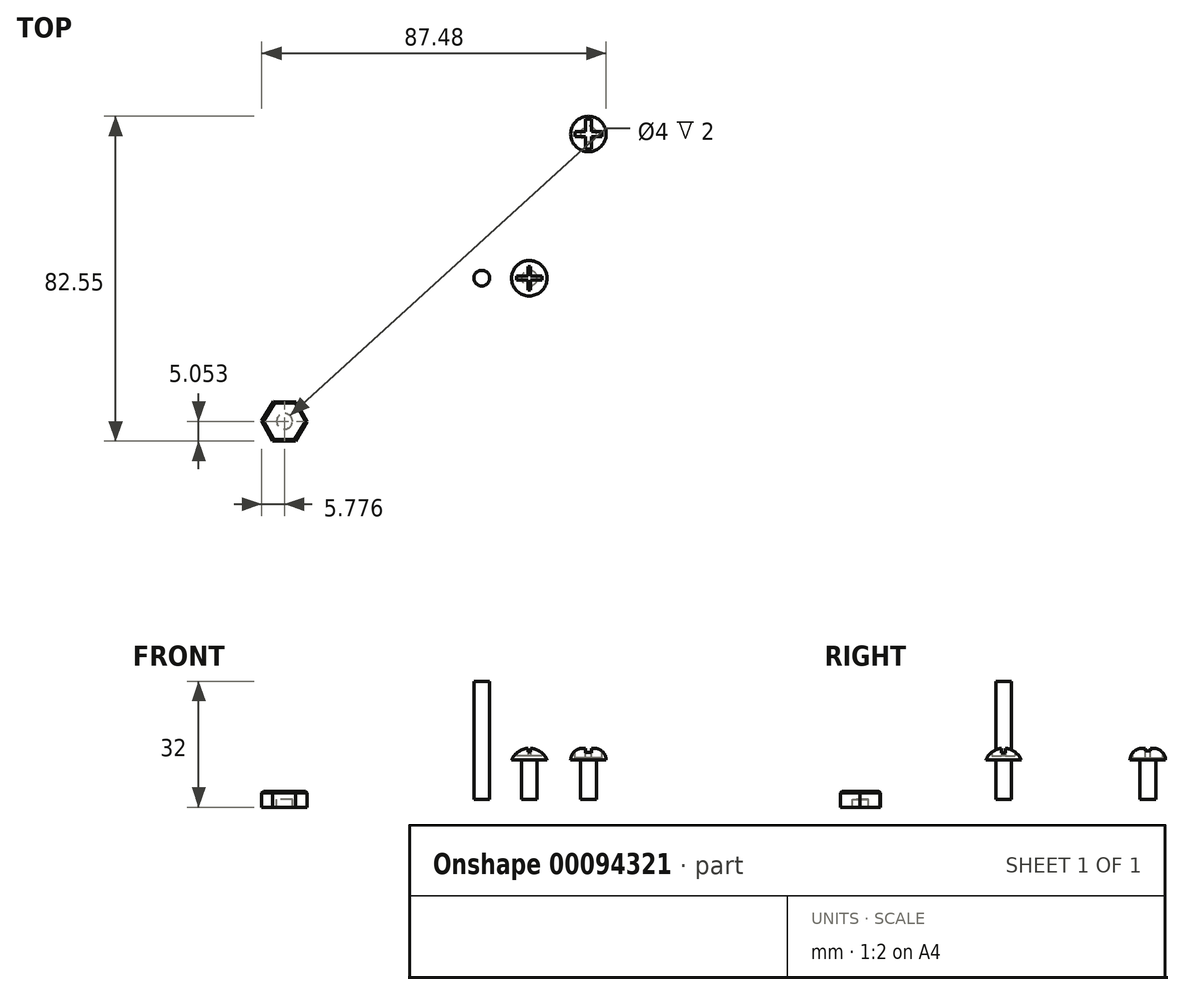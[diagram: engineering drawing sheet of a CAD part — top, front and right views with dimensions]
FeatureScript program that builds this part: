
annotation { "Feature Type Name" : "Feature", "Feature Type Description" : "" }
export const myFeature = defineFeature(function(context is Context, id is Id, definition is map)
    precondition{}
    {
        {
            var Q0;
            Q0=qCreatedBy(makeId("Top.planeOp"),FACE);
            var sketch = newSketch(context, id + "F0", { "sketchPlane" : qUnion([Q0])});
            skCircle(sketch, "E0", {"center": v(0, 0) * mm, "radius": 2 * mm});
            skSolve(sketch);
        }
        {
            var Q0;
            Q0 = qSketchRegion(id + "F0", true);
            extrude(context, id + "F1", {"entities" : qUnion([Q0]), "depth" : 30 * mm});
        }
        {
            var Q0;
            Q0=qCreatedBy(makeId("Top.planeOp"),FACE);
            var sketch = newSketch(context, id + "F2", { "sketchPlane" : qUnion([Q0])});
            skCircle(sketch, "E1.cCircle", {"center": v(-50.11, -36.36) * mm, "radius": 5 * mm, "construction": true});
            skLineSegment(sketch, "E1.0", {"start": v(-47.13, -31.41) * mm, "end": v(-44.34, -36.47) * mm});
            skLineSegment(sketch, "E1.1", {"start": v(-44.34, -36.47) * mm, "end": v(-47.32, -41.41) * mm});
            skLineSegment(sketch, "E1.2", {"start": v(-47.32, -41.41) * mm, "end": v(-53.1, -41.3) * mm});
            skLineSegment(sketch, "E1.3", {"start": v(-53.1, -41.3) * mm, "end": v(-55.89, -36.24) * mm});
            skLineSegment(sketch, "E1.4", {"start": v(-55.89, -36.24) * mm, "end": v(-52.9, -31.3) * mm});
            skLineSegment(sketch, "E1.5", {"start": v(-52.9, -31.3) * mm, "end": v(-47.13, -31.41) * mm});
            skPoint(sketch, "E1.0.midPoint", {"position": v(-45.74, -33.94) * mm});
            skSolve(sketch);
        }
        {
            var Q0;
            Q0 = qSketchRegion(id + "F2", true);
            extrude(context, id + "F3", {"entities" : qUnion([Q0]), "endBound" : BoundingType.SYMMETRIC, "oppositeDirection" : true, "depth" : 4 * mm});
        }
        {
            var Q0;
            Q0=makeQuery(id+"F3.opExtrude","CAP_FACE",FACE,{"disambiguationData":[OSD([sQuery(id+"F2.wireOp",EDGE,"E1.0"),sQuery(id+"F2.wireOp",EDGE,"E1.1"),sQuery(id+"F2.wireOp",EDGE,"E1.2"),sQuery(id+"F2.wireOp",EDGE,"E1.3"),sQuery(id+"F2.wireOp",EDGE,"E1.4"),sQuery(id+"F2.wireOp",EDGE,"E1.5")])],"isStart":true});
            var sketch = newSketch(context, id + "F4", { "sketchPlane" : qUnion([Q0])});
            skArc(sketch, "E2", {"start": v(-50.11, -40.36) * mm, "mid": v(-46.11, -36.36) * mm, "end": v(-50.11, -32.36) * mm});
            skLineSegment(sketch, "E3", {"start": v(-50.11, -32.36) * mm, "end": v(-50.11, -40.36) * mm, "construction": true});
            skSolve(sketch);
        }
        {
            var Q0;
            Q0=sQuery(id+"F4.wireOp",EDGE,"E2");
            var Q1;
            Q1=sQuery(id+"F4.wireOp",EDGE,"E3");
            revolve(context, id + "F5", {"bodyType" : ToolBodyType.SURFACE, "surfaceEntities" : qUnion([Q0]), "axis" : qUnion([Q1]), "revolveType" : RevolveType.ONE_DIRECTION, "angle" : 180 * degree});
        }
        {
            var Q0;
            Q0=makeQuery(id+"F2.imprint","IMPRINT",FACE,{"disambiguationData":[TD([[makeQuery(id+"F2.imprint","IMPRINT",EDGE,{"derivedFrom":sQuery(id+"F2.wireOp",EDGE,"E1.0")}),-1.0]])]});
            var sketch = newSketch(context, id + "F6", { "sketchPlane" : qUnion([Q0])});
            skCircle(sketch, "E4", {"center": v(-50.11, -36.36) * mm, "radius": 2 * mm});
            skSolve(sketch);
        }
        {
            var Q0;
            Q0 = qSketchRegion(id + "F6", true);
            extrude(context, id + "F7", {"entities" : qUnion([Q0]), "operationType" : NewBodyOperationType.REMOVE, "oppositeDirection" : true, "depth" : 25 * mm});
        }
        {
            var Q0;
            Q0=qCreatedBy(makeId("Top.planeOp"),FACE);
            var sketch = newSketch(context, id + "F8", { "sketchPlane" : qUnion([Q0])});
            skCircle(sketch, "E5", {"center": v(27.1, 36.64) * mm, "radius": 2 * mm});
            skSolve(sketch);
        }
        {
            var Q0;
            Q0 = qSketchRegion(id + "F8", true);
            extrude(context, id + "F9", {"entities" : qUnion([Q0]), "depth" : 10 * mm});
        }
        {
            var Q0;
            Q0=makeQuery(id+"F9.opExtrude","CAP_FACE",FACE,{"disambiguationData":[OSD([sQuery(id+"F8.wireOp",EDGE,"E5")])],"isStart":false});
            var sketch = newSketch(context, id + "F10", { "sketchPlane" : qUnion([Q0])});
            skCircle(sketch, "E6", {"center": v(27.1, 36.64) * mm, "radius": 4.5 * mm});
            skSolve(sketch);
        }
        {
            var Q0;
            Q0 = qSketchRegion(id + "F10", true);
            extrude(context, id + "F11", {"entities" : qUnion([Q0]), "operationType" : NewBodyOperationType.ADD, "depth" : 3 * mm});
        }
        {
            var Q0;
            Q0=makeQuery(id+"F11.opExtrude","CAP_EDGE",EDGE,{"disambiguationData":[OSD([sQuery(id+"F10.wireOp",EDGE,"E6")])],"isStart":false});
            fillet(context, id + "F12", {"entities" : qUnion([Q0]), "radius" : 3 * mm, "tangentPropagation" : true, "allowEdgeOverflow" : false});
        }
        {
            var Q0;
            Q0=makeQuery(id+"F11.opExtrude","CAP_FACE",FACE,{"disambiguationData":[OSD([sQuery(id+"F10.wireOp",EDGE,"E6")])],"isStart":false});
            var sketch = newSketch(context, id + "F13", { "sketchPlane" : qUnion([Q0])});
            skLineSegment(sketch, "E7.bottom", {"start": v(27.84, 32.86) * mm, "end": v(26.34, 32.86) * mm});
            skLineSegment(sketch, "E7.top", {"start": v(27.84, 40.42) * mm, "end": v(26.34, 40.42) * mm});
            skLineSegment(sketch, "E7.left", {"start": v(27.84, 32.86) * mm, "end": v(27.84, 40.42) * mm});
            skLineSegment(sketch, "E7.right", {"start": v(26.34, 32.86) * mm, "end": v(26.34, 40.42) * mm});
            skPoint(sketch, "E7.middle", {"position": v(27.1, 36.64) * mm});
            skLineSegment(sketch, "E8.bottom", {"start": v(30.5, 36.04) * mm, "end": v(23.7, 36.04) * mm});
            skLineSegment(sketch, "E8.top", {"start": v(30.5, 37.24) * mm, "end": v(23.7, 37.24) * mm});
            skLineSegment(sketch, "E8.left", {"start": v(30.5, 36.04) * mm, "end": v(30.5, 37.24) * mm});
            skLineSegment(sketch, "E8.right", {"start": v(23.7, 36.04) * mm, "end": v(23.7, 37.24) * mm});
            skSolve(sketch);
        }
        {
            var Q0;
            Q0 = qSketchRegion(id + "F13", true);
            extrude(context, id + "F14", {"entities" : qUnion([Q0]), "operationType" : NewBodyOperationType.REMOVE, "oppositeDirection" : true, "depth" : 2.41 * mm});
        }
        {
            var Q0;
            Q0=makeQuery(id+"F3.opExtrude","CAP_EDGE",EDGE,{"disambiguationData":[OSD([sQuery(id+"F2.wireOp",EDGE,"E1.4")])],"isStart":true});
            var Q1;
            Q1=makeQuery(id+"F3.opExtrude","CAP_EDGE",EDGE,{"disambiguationData":[OSD([sQuery(id+"F2.wireOp",EDGE,"E1.5")])],"isStart":true});
            var Q2;
            Q2=makeQuery(id+"F3.opExtrude","CAP_EDGE",EDGE,{"disambiguationData":[OSD([sQuery(id+"F2.wireOp",EDGE,"E1.0")])],"isStart":true});
            var Q3;
            Q3=makeQuery(id+"F3.opExtrude","CAP_EDGE",EDGE,{"disambiguationData":[OSD([sQuery(id+"F2.wireOp",EDGE,"E1.3")])],"isStart":true});
            var Q4;
            Q4=makeQuery(id+"F3.opExtrude","CAP_EDGE",EDGE,{"disambiguationData":[OSD([sQuery(id+"F2.wireOp",EDGE,"E1.2")])],"isStart":true});
            var Q5;
            Q5=makeQuery(id+"F3.opExtrude","CAP_EDGE",EDGE,{"disambiguationData":[OSD([sQuery(id+"F2.wireOp",EDGE,"E1.1")])],"isStart":true});
            chamfer(context, id + "F15", {"entities" : qUnion([Q0, Q1, Q2, Q3, Q4, Q5]), "width" : 0.4 * mm, "tangentPropagation" : true});
        }
        {
            var Q0;
            Q0=qCreatedBy(makeId("Front.planeOp"),FACE);
            var sketch = newSketch(context, id + "F16", { "sketchPlane" : qUnion([Q0])});
            skLineSegment(sketch, "E9", {"start": v(12.08, 0) * mm, "end": v(12.08, 13) * mm});
            skLineSegment(sketch, "E10", {"start": v(12.08, 10) * mm, "end": v(7.58, 10) * mm, "construction": true});
            skArc(sketch, "E11", {"start": v(12.08, 13) * mm, "mid": v(9.38, 12.18) * mm, "end": v(7.58, 10) * mm});
            skLineSegment(sketch, "E12", {"start": v(7.58, 10) * mm, "end": v(10.08, 10) * mm});
            skLineSegment(sketch, "E13", {"start": v(10.08, 10) * mm, "end": v(10.08, 0) * mm});
            skLineSegment(sketch, "E14", {"start": v(10.08, 0) * mm, "end": v(12.08, 0) * mm});
            skPoint(sketch, "E15.orphan", {"position": v(16.58, 10) * mm});
            skLineSegment(sketch, "E16", {"start": v(12.08, 15.56) * mm, "end": v(12.08, -4.15) * mm, "construction": true});
            skSolve(sketch);
        }
        {
            var Q0;
            Q0=makeQuery(id+"F16.imprint","IMPRINT",FACE,{"disambiguationData":[TD([[makeQuery(id+"F16.imprint","IMPRINT",EDGE,{"derivedFrom":sQuery(id+"F16.wireOp",EDGE,"E9")}),1.0]])]});
            var Q1;
            Q1=sQuery(id+"F16.wireOp",EDGE,"E16");
            var Q2;
            Q2=sQuery(id+"F16.wireOp",EDGE,"E16");
            revolve(context, id + "F17", {"entities" : qUnion([Q0]), "surfaceEntities" : qUnion([Q1]), "axis" : qUnion([Q2]), "revolveType" : RevolveType.FULL});
        }
        {
            var Q0;
            Q0=makeQuery(id+"F17.opRevolve","SWEPT_FACE",FACE,{"disambiguationData":[OSD([sQuery(id+"F16.wireOp",EDGE,"E12")])]});
            var sketch = newSketch(context, id + "F18", { "sketchPlane" : qUnion([Q0])});
            skLineSegment(sketch, "E17.bottom", {"start": v(12.4, 2.95) * mm, "end": v(11.76, 2.95) * mm});
            skLineSegment(sketch, "E17.top", {"start": v(12.4, -2.95) * mm, "end": v(11.76, -2.95) * mm});
            skLineSegment(sketch, "E17.left", {"start": v(12.4, 2.95) * mm, "end": v(12.4, 0.52) * mm});
            skLineSegment(sketch, "E17.right", {"start": v(11.76, 2.95) * mm, "end": v(11.76, 0.52) * mm});
            skPoint(sketch, "E17.middle", {"position": v(12.08, 0) * mm});
            skLineSegment(sketch, "E18.bottom", {"start": v(15.3, -0.52) * mm, "end": v(12.4, -0.52) * mm});
            skLineSegment(sketch, "E18.top", {"start": v(15.3, 0.52) * mm, "end": v(12.4, 0.52) * mm});
            skLineSegment(sketch, "E18.left", {"start": v(15.3, -0.52) * mm, "end": v(15.3, 0.52) * mm});
            skLineSegment(sketch, "E18.right", {"start": v(8.86, -0.52) * mm, "end": v(8.86, 0.52) * mm});
            skLineSegment(sketch, "E19.trimOffspring", {"start": v(11.76, -0.52) * mm, "end": v(11.76, -2.95) * mm});
            skLineSegment(sketch, "E20.trimOffspring", {"start": v(11.76, 0.52) * mm, "end": v(8.86, 0.52) * mm});
            skLineSegment(sketch, "E21.trimOffspring", {"start": v(12.4, -0.52) * mm, "end": v(12.4, -2.95) * mm});
            skLineSegment(sketch, "E22.trimOffspring", {"start": v(11.76, -0.52) * mm, "end": v(8.86, -0.52) * mm});
            skSolve(sketch);
        }
        {
            var Q0;
            {var subQ0=sQuery(id+"F18.wireOp",EDGE,"E17.bottom");Q0=makeQuery(id+"F18.imprint","IMPRINT",FACE,{"disambiguationData":[TD([[makeQuery(id+"F18.imprint","IMPRINT",EDGE,{"derivedFrom":subQ0}),1.0]])]});}
            var Q1;
            {var subQ0=sQuery(id+"F18.wireOp",EDGE,"E17.top");Q1=makeQuery(id+"F18.imprint","IMPRINT",FACE,{"disambiguationData":[TD([[makeQuery(id+"F18.imprint","IMPRINT",EDGE,{"derivedFrom":subQ0}),-1.0]])]});}
            var Q2;
            {var subQ0=sQuery(id+"F18.wireOp",EDGE,"E18.left");Q2=makeQuery(id+"F18.imprint","IMPRINT",FACE,{"disambiguationData":[TD([[makeQuery(id+"F18.imprint","IMPRINT",EDGE,{"derivedFrom":subQ0}),1.0]])]});}
            var Q3;
            {var subQ0=sQuery(id+"F18.wireOp",EDGE,"E18.right");Q3=makeQuery(id+"F18.imprint","IMPRINT",FACE,{"disambiguationData":[TD([[makeQuery(id+"F18.imprint","IMPRINT",EDGE,{"derivedFrom":subQ0}),-1.0]])]});}
            var Q4;
            {var subQ3=sQuery(id+"F18.wireOp",EDGE,"E18.top");var subQ17=sQuery(id+"F18.wireOp",EDGE,"E17.left");var subQ18=makeQuery(id+"F18.imprint","INTERSECT",VERTEX,{"derivedFrom":[subQ17,subQ3]});Q4=makeQuery(id+"F18.imprint","IMPRINT",FACE,{"disambiguationData":[TD([[makeQuery(id+"F18.imprint","IMPRINT",EDGE,{"disambiguationData":[TD([[subQ18,1.0]])],"derivedFrom":subQ17}),-1.0]])]});}
            extrude(context, id + "F19", {"entities" : qUnion([Q0, Q1, Q2, Q3, Q4]), "operationType" : NewBodyOperationType.REMOVE, "endBound" : BoundingType.THROUGH_ALL, "oppositeDirection" : true, "depth" : 25 * mm, "hasSecondDirection" : true, "secondDirectionOppositeDirection" : true, "secondDirectionDepth" : 1 * mm});
        }
    });
